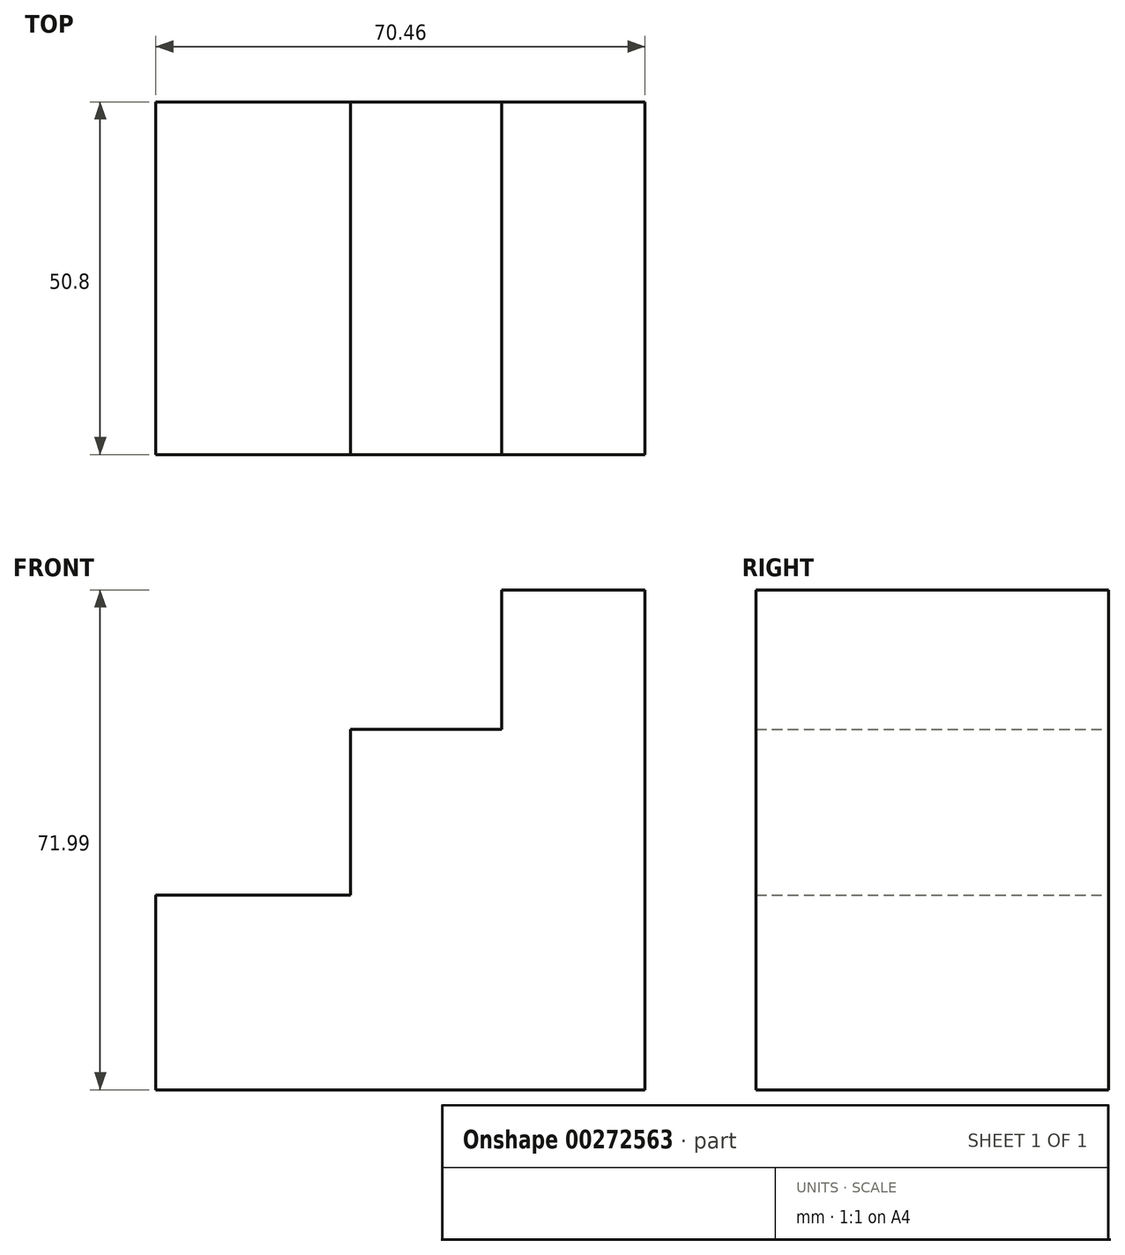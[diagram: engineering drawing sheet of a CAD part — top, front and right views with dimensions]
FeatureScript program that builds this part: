
annotation { "Feature Type Name" : "Feature", "Feature Type Description" : "" }
export const myFeature = defineFeature(function(context is Context, id is Id, definition is map)
    precondition{}
    {
        {
            var Q0;
            Q0=qCreatedBy(makeId("Front.planeOp"),FACE);
            var sketch = newSketch(context, id + "F0", { "sketchPlane" : qUnion([Q0])});
            skLineSegment(sketch, "E0", {"start": v(0, 0) * mm, "end": v(70.46, 0) * mm});
            skLineSegment(sketch, "E1", {"start": v(70.46, 0) * mm, "end": v(70.46, 71.99) * mm});
            skLineSegment(sketch, "E2", {"start": v(70.46, 71.99) * mm, "end": v(49.84, 71.99) * mm});
            skLineSegment(sketch, "E3", {"start": v(49.84, 71.99) * mm, "end": v(49.84, 51.94) * mm});
            skLineSegment(sketch, "E4", {"start": v(49.84, 51.94) * mm, "end": v(28.07, 51.94) * mm});
            skLineSegment(sketch, "E5", {"start": v(28.07, 51.94) * mm, "end": v(28.07, 28.07) * mm});
            skLineSegment(sketch, "E6", {"start": v(28.07, 28.07) * mm, "end": v(0, 28.07) * mm});
            skLineSegment(sketch, "E7", {"start": v(0, 28.07) * mm, "end": v(0, 0) * mm});
            skSolve(sketch);
        }
        {
            var Q0;
            Q0 = qSketchRegion(id + "F0", true);
            extrude(context, id + "F1", {"entities" : qUnion([Q0]), "depth" : 50.8 * mm});
        }
    });
